FCSTD DOCUMENT  (FreeCAD 0.18R16146 (Git))
Label: full_parametric_model90
License: All rights reserved
LicenseURL: http://en.wikipedia.org/wiki/All_rights_reserved
objects: Part::FeaturePython×27, Sketcher::SketchObject×13, PartDesign::Pad×5, Part::MultiFuse×5, Part::Extrusion×5, Part::Cut×4, App::DocumentObjectGroup×4, Mesh::Feature×4, Part::Mirroring×4, Part::MultiCommon×3, PartDesign::Revolution×3, Part::Feature×3, Part::Compound×2, Part::Fillet×2, Part::Cylinder×1, Spreadsheet::Sheet×1, Part::Sphere×1, Part::Chamfer×1, Part::Loft×1
note: 88 computed .brp shape members not serialized (recipe doc carries the construction recipe); baked Part::Feature solids carry a one-line shape summary decoded from their .brp

FEATURE [Part::Cylinder] Cylinder
  Angle = 360
  AttacherType = Attacher::AttachEngine3D
  Height = 10.3
  Placement = pos=(0,0,-5.15) rot=(0,0,1;0rad)
  Radius = 5.5
  expr: Height = Spreadsheet.SpacerDepth
  expr: Radius = Spreadsheet.SpacerD / 2
FEATURE [Sketcher::SketchObject] Sketch004  label="SpacerTailsSketch"
  MapMode = 5
  expr: Constraints.AxeOutR = Spreadsheet.AxisD / 2 + Spreadsheet.SpacerMinThickness
  expr: Constraints.MaxR = Spreadsheet.SpacerTailsD / 2
  expr: Constraints.AxeR = Spreadsheet.AxisD / 2
  sketch-geometry (15):
    g0: ArcOfCircle CenterX=0 CenterY=0 CenterZ=0 NormalX=0 NormalY=0 NormalZ=1 AngleXU=0 Radius=9 StartAngle=1.8326 EndAngle=2.35619
    g1: Circle [constr] CenterX=0 CenterY=0 CenterZ=0 NormalX=0 NormalY=0 NormalZ=1 AngleXU=0 Radius=9
    g2: ArcOfCircle CenterX=11.5897 CenterY=20.074 CenterZ=0 NormalX=0 NormalY=0 NormalZ=1 AngleXU=0 Radius=17.9795 StartAngle=3.82699 EndAngle=4.55059
    g3: Circle [constr] CenterX=0 CenterY=0 CenterZ=0 NormalX=0 NormalY=0 NormalZ=1 AngleXU=0 Radius=5.2
    g4: LineSegment [constr] StartX=0 StartY=0 StartZ=0 EndX=2.6 EndY=4.50333 EndZ=0
    g5: ArcOfCircle CenterX=0 CenterY=0 CenterZ=0 NormalX=0 NormalY=0 NormalZ=1 AngleXU=0 Radius=9 StartAngle=6.02139 EndAngle=6.54498
    g6: ArcOfCircle CenterX=11.5897 CenterY=-20.074 CenterZ=0 NormalX=0 NormalY=0 NormalZ=1 AngleXU=0 Radius=17.9795 StartAngle=1.7326 EndAngle=2.45619
    g7: LineSegment [constr] StartX=0 StartY=0 StartZ=0 EndX=2.6 EndY=-4.50333 EndZ=0
    g8: ArcOfCircle CenterX=0 CenterY=0 CenterZ=0 NormalX=0 NormalY=0 NormalZ=1 AngleXU=0 Radius=9 StartAngle=3.92699 EndAngle=4.45059
    g9: LineSegment [constr] StartX=0 StartY=0 StartZ=0 EndX=-5.2 EndY=0 EndZ=0
    g10: LineSegment [constr] StartX=0 StartY=0 StartZ=0 EndX=-6.36396 EndY=6.36396 EndZ=0
    g11: ArcOfCircle CenterX=-23.1795 CenterY=2e-12 CenterZ=0 NormalX=0 NormalY=0 NormalZ=1 AngleXU=0 Radius=17.9795 StartAngle=5.92139 EndAngle=6.64498
    g12: LineSegment [constr] StartX=0 StartY=0 StartZ=0 EndX=-6.36396 EndY=-6.36396 EndZ=0
    g13: LineSegment [constr] StartX=0 StartY=0 StartZ=0 EndX=8.69333 EndY=-2.32937 EndZ=0
    g14: Circle CenterX=0 CenterY=0 CenterZ=0 NormalX=0 NormalY=0 NormalZ=1 AngleXU=0 Radius=4
  constraints (43):
    c: Coincident(g0,g-1)
    c: Angle(g0) = 0.523599
    c: Coincident(g1,g-1)
    c: Radius(g1) = 9  'MaxR'
    c: PointOnObject(g0,g1)
    c: Coincident(g2,g0)
    c: PointOnObject(g2,g1)
    c: Coincident(g3,g-1)
    c: Radius(g3) = 5.2  'AxeOutR'
    c: Coincident(g4,g-1)
    c: PointOnObject(g4,g3)
    c: PointOnObject(g4,g2)
    c: Angle(g5) = 0.523599
    c: Coincident(g5,g2)
    c: PointOnObject(g5,g1)
    c: Coincident(g6,g5)
    c: Coincident(g-1,g5)
    c: Coincident(g7,g-1)
    c: PointOnObject(g7,g3)
    c: PointOnObject(g7,g6)
    c: Coincident(g8,g-1)
    c: Coincident(g8,g6)
    c: PointOnObject(g8,g1)
    c: Angle(g8) = 0.523599
    c: Angle(g7,g4) = 2.0944
    c: Coincident(g9,g-1)
    c: PointOnObject(g9,g3)
    c: Angle(g9,g7) = 2.0944
    c: Coincident(g10,g-1)
    c: Coincident(g10,g0)
    c: Angle(g4,g10) = 1.309
    c: Coincident(g11,g8)
    c: Coincident(g11,g0)
    c: PointOnObject(g9,g11)
    c: Coincident(g12,g-1)
    c: Coincident(g12,g8)
    c: Angle(g10,g12) = 1.5708
    c: Coincident(g13,g-1)
    c: Coincident(g13,g5)
    c: Angle(g12,g13) = 2.0944
    c: Coincident(g14,g-1)
    c: Radius(g14) = 4  'AxeR'
    c: Angle(g-1,g9) = 3.14159  'Rotation'
FEATURE [PartDesign::Pad] Pad003  label="SpacerTails"
  Length = 1.4
  Length2 = 100
  Midplane = true
  Profile = -> Sketch004
  Type = 0
  expr: Length = Spreadsheet.SpacerTailsDepth
FEATURE [Spreadsheet::Sheet] Spreadsheet
  cells = A1=Диаметр оси; B1(AxisD)=8; C1=мм; A2=Наружный диаметр подшипника; B2(BearingD)=16; C2=мм; A3=Шаг звена; B3(LinkLength)=40; C3=мм; A4=Минимальный угол складывания; B4(MinLinkAngle)=90; C4=градусов; A5=Толщина подшипника; B5(BearingDepth)=5; C5=мм; A6=Минимальная ширина; B6(MinWidth)=3; C6=мм; A7=Минимальный отступ; B7(MinSpacing)=1; C7=мм; A8=Скругление углов; B8(FIlletR)=2; C8=мм; A9=Держащий край; B9(HoldingEdge)=1.2; C9=мм; A10=Наружный диаметр втулки; B10(SpacerD)=11; C10=мм; A11=Глубина втулки; B11(SpacerDepth)=10.3; C11=мм; A12=Толщина хвостиков втулки; B12(SpacerTailsDepth)=1.4; C12=мм; A13=Диаметр втулки по хвостикам; B13(SpacerTailsD)=18; C13=мм; A14=Минимальная толщина втулки; B14(SpacerMinThickness)=1.2; C14=мм; A15=Клиренс отверстий; B15(HolesClearance)=0.1; C15=мм; A16=Угол оптимального эллипса; B16(OptimalEllipseAngle)=56.33131818071931; C16=градусов; A17=Y-позиция центра направляющей; B17(RailCenterY)==LinkLength * sin(OptimalEllipseAngle)
FEATURE [Part::FeaturePython] Clone007  label="SpacerTailsCutter"  # Draft clone (typed FeaturePython)
  Objects = -> [Pad003]
  Scale = (1,1,8.09286)
  expr: Scale.z = 1.1 * Spreadsheet.SpacerDepth / Spreadsheet.SpacerTailsDepth
FEATURE [Part::MultiCommon] Common
  Shapes = -> [Cylinder,Clone007]
FEATURE [Part::MultiFuse] Fusion  label="SpacerPart"
  Shapes = -> [Common,Pad003]
FEATURE [Sketcher::SketchObject] Sketch013  label="BallBearingInnerRingSketch"
  MapMode = 5
  Placement = pos=(0,0,0) rot=(1,0,0;1.5708rad)
  expr: Constraints[11] = Spreadsheet.AxisD / 2 + (Spreadsheet.BearingD - Spreadsheet.AxisD) / 6
  expr: Constraints[10] = Spreadsheet.AxisD / 2
  expr: Constraints[9] = Spreadsheet.BearingDepth
  sketch-geometry (4):
    g0: LineSegment StartX=4 StartY=2.5 StartZ=0 EndX=5.33333 EndY=2.5 EndZ=0
    g1: LineSegment StartX=5.33333 StartY=2.5 StartZ=0 EndX=5.33333 EndY=-2.5 EndZ=0
    g2: LineSegment StartX=5.33333 StartY=-2.5 StartZ=0 EndX=4 EndY=-2.5 EndZ=0
    g3: LineSegment StartX=4 StartY=-2.5 StartZ=0 EndX=4 EndY=2.5 EndZ=0
  constraints (12):
    c: Coincident(g0,g1)
    c: Coincident(g1,g2)
    c: Coincident(g2,g3)
    c: Coincident(g3,g0)
    c: Horizontal(g0)
    c: Horizontal(g2)
    c: Vertical(g1)
    c: Vertical(g3)
    c: Symmetric(g0,g2,g-1)
    c: DistanceY(g2,g0) = 5
    c: DistanceX(g0) = 4
    c: DistanceX(g0) = 5.33333
FEATURE [PartDesign::Revolution] Revolution  label="BallBearingInnerRing"
  Angle = 360
  Axis = (0,2e-16,1)
  Base = (0,0,0)
  Placement = pos=(0,0,0) rot=(1,0,0;1.5708rad)
  Profile = -> Sketch013
  ReferenceAxis = -> Sketch013 [V_Axis]
  Reversed = true
FEATURE [Sketcher::SketchObject] Sketch014  label="BallBearingInnerRingSketch001"
  MapMode = 5
  Placement = pos=(0,0,0) rot=(1,0,0;1.5708rad)
  expr: Constraints[11] = Spreadsheet.BearingD / 2 - (Spreadsheet.BearingD - Spreadsheet.AxisD) / 6
  expr: Constraints[10] = Spreadsheet.BearingD / 2
  expr: Constraints[9] = Spreadsheet.BearingDepth
  sketch-geometry (4):
    g0: LineSegment StartX=8 StartY=2.5 StartZ=0 EndX=6.66667 EndY=2.5 EndZ=0
    g1: LineSegment StartX=6.66667 StartY=2.5 StartZ=0 EndX=6.66667 EndY=-2.5 EndZ=0
    g2: LineSegment StartX=6.66667 StartY=-2.5 StartZ=0 EndX=8 EndY=-2.5 EndZ=0
    g3: LineSegment StartX=8 StartY=-2.5 StartZ=0 EndX=8 EndY=2.5 EndZ=0
  constraints (12):
    c: Coincident(g0,g1)
    c: Coincident(g1,g2)
    c: Coincident(g2,g3)
    c: Coincident(g3,g0)
    c: Horizontal(g0)
    c: Horizontal(g2)
    c: Vertical(g1)
    c: Vertical(g3)
    c: Symmetric(g0,g2,g-1)
    c: DistanceY(g2,g0) = 5
    c: DistanceX(g0) = 8
    c: DistanceX(g0) = 6.66667
FEATURE [PartDesign::Revolution] Revolution001  label="BallBearingOuterRing"
  Angle = 360
  Axis = (0,2e-16,1)
  Base = (0,0,0)
  Placement = pos=(0,0,0) rot=(1,0,0;1.5708rad)
  Profile = -> Sketch014
  ReferenceAxis = -> Sketch014 [V_Axis]
  Reversed = true
FEATURE [Sketcher::SketchObject] Sketch015  label="BallBearingGrooveTorusSketch"
  MapMode = 5
  Placement = pos=(0,0,0) rot=(1,0,0;1.5708rad)
  expr: Constraints[1] = 2 * (Spreadsheet.BearingD - Spreadsheet.AxisD) / 12
  sketch-geometry (1):
    g0: Circle CenterX=6 CenterY=0 CenterZ=0 NormalX=0 NormalY=0 NormalZ=1 AngleXU=0 Radius=1.33333
  constraints (3):
    c: PointOnObject(g0,g-1)
    c: Radius(g0) = 1.33333
    c: DistanceX(g0) = 6
FEATURE [PartDesign::Revolution] Revolution002  label="BallBearingGrooveTorus"
  Angle = 360
  Axis = (0,2e-16,1)
  Base = (0,0,0)
  Placement = pos=(0,0,0) rot=(1,0,0;1.5708rad)
  Profile = -> Sketch015
  ReferenceAxis = -> Sketch015 [V_Axis]
  Reversed = true
FEATURE [Part::MultiFuse] Fusion001  label="BallBearingRings"
  Shapes = -> [Revolution001,Revolution]
FEATURE [Part::Cut] Cut  label="BallBearingRingsWithGroove"
  Base = -> Fusion001
  Tool = -> Revolution002
FEATURE [Part::Sphere] Sphere
  Angle1 = -90
  Angle2 = 90
  Angle3 = 360
  AttacherType = Attacher::AttachEngine3D
  Placement = pos=(6,0,0) rot=(0,0,1;0rad)
  Radius = 1.33333
  expr: Placement.Base.x = (Spreadsheet.BearingD + Spreadsheet.AxisD) / 4
FEATURE [Part::FeaturePython] Array  # Draft array (typed FeaturePython)
  Angle = 360
  ArrayType = 1
  Axis = (0,0,1)
  Base = -> Sphere
  Center = (0,0,0)
  Fuse = false
  IntervalAxis = (0,0,0)
  IntervalX = (1,0,0)
  IntervalY = (0,1,0)
  IntervalZ = (0,0,0)
  NumberPolar = 10
  NumberX = 2
  NumberY = 2
  NumberZ = 1
FEATURE [Part::MultiFuse] Fusion002  label="BallBearing"
  Shapes = -> [Array,Cut]
FEATURE [App::DocumentObjectGroup] Group  label="StockParts"
  Group = -> [Fusion,Fusion002]
FEATURE [Part::Feature] Path  label="Path16D40L"
  Placement = pos=(-54.1756,58.5806,12.8) rot=(0,0,1;0rad)
  shape: bbox 108.4 x 50.58 x 2e-07 mm, 0 faces, 0 solids (baked)
  expr: Placement.Base.y = 2 * Spreadsheet.RailCenterY - 16 / 2
  expr: Placement.Base.x = 16 / 2 - Spreadsheet.LinkLength * (1 + cos(Spreadsheet.OptimalEllipseAngle))
FEATURE [Part::FeaturePython] Clone023  label="CenterBearing"  # Draft clone (typed FeaturePython)
  Objects = -> [Fusion002]
  Scale = (1,1,1)
FEATURE [Part::FeaturePython] Clone024  label="LeftBearing"  # Draft clone (typed FeaturePython)
  Objects = -> [Fusion002]
  Placement = pos=(0,0,15.3) rot=(0,0,1;0rad)
  Scale = (1,1,1)
  expr: Placement.Base.z = Spreadsheet.SpacerDepth + Spreadsheet.BearingDepth
FEATURE [Part::FeaturePython] Clone025  label="RightBearing"  # Draft clone (typed FeaturePython)
  Objects = -> [Fusion002]
  Placement = pos=(0,0,-15.3) rot=(0,0,1;0rad)
  Scale = (1,1,1)
  expr: Placement.Base.z = -Spreadsheet.SpacerDepth - Spreadsheet.BearingDepth
FEATURE [Part::FeaturePython] Clone026  label="LeftSpacer"  # Draft clone (typed FeaturePython)
  Objects = -> [Fusion]
  Placement = pos=(0,0,7.65) rot=(0,0,1;0rad)
  Scale = (1,1,1)
  expr: Placement.Base.z = (Spreadsheet.SpacerDepth + Spreadsheet.BearingDepth) / 2
FEATURE [Part::FeaturePython] Clone027  label="RightSpacer"  # Draft clone (typed FeaturePython)
  Objects = -> [Fusion]
  Placement = pos=(0,0,-7.65) rot=(0,0,1;0rad)
  Scale = (1,1,1)
  expr: Placement.Base.z = -0.5 * (Spreadsheet.SpacerDepth + Spreadsheet.BearingDepth)
FEATURE [Sketcher::SketchObject] Sketch012007  label="TrussSketch"
  MapMode = 5
  Placement = pos=(0,0,0) rot=(1,0,0;1.5708rad)
  expr: Constraints[36] = 0.5 * (Spreadsheet.BearingDepth + Spreadsheet.SpacerDepth + Spreadsheet.SpacerTailsDepth) + Spreadsheet.MinSpacing
  expr: Constraints[35] = Spreadsheet.HoldingEdge * 2
  sketch-geometry (14):
    g0: LineSegment StartX=11.0471 StartY=9.35 StartZ=0 EndX=1.69706 EndY=0 EndZ=0
    g1: LineSegment StartX=1.69706 StartY=0 StartZ=0 EndX=11.0471 EndY=-9.35 EndZ=0
    g2: LineSegment StartX=11.0471 StartY=-9.35 StartZ=0 EndX=11.0471 EndY=9.35 EndZ=0
    g3: LineSegment StartX=-1.69706 StartY=0 StartZ=0 EndX=-11.0471 EndY=9.35 EndZ=0
    g4: LineSegment StartX=-11.0471 StartY=9.35 StartZ=0 EndX=-11.0471 EndY=-9.35 EndZ=0
    g5: LineSegment StartX=-11.0471 StartY=-9.35 StartZ=0 EndX=-1.69706 EndY=0 EndZ=0
    g6: LineSegment StartX=0 StartY=1.69706 StartZ=0 EndX=7.65294 EndY=9.35 EndZ=0
    g7: LineSegment StartX=7.65294 StartY=9.35 StartZ=0 EndX=-7.65294 EndY=9.35 EndZ=0
    g8: LineSegment StartX=-7.65294 StartY=9.35 StartZ=0 EndX=0 EndY=1.69706 EndZ=0
    g9: LineSegment [constr] StartX=11.0471 StartY=9.35 StartZ=0 EndX=7.65294 EndY=9.35 EndZ=0
    g10: LineSegment [constr] StartX=-1.69706 StartY=0 StartZ=0 EndX=0 EndY=1.69706 EndZ=0
    g11: LineSegment StartX=-7.65294 StartY=-9.35 StartZ=0 EndX=0 EndY=-1.69706 EndZ=0
    g12: LineSegment StartX=0 StartY=-1.69706 StartZ=0 EndX=7.65294 EndY=-9.35 EndZ=0
    g13: LineSegment StartX=7.65294 StartY=-9.35 StartZ=0 EndX=-7.65294 EndY=-9.35 EndZ=0
  constraints (37):
    c: PointOnObject(g0,g-1)
    c: Coincident(g0,g1)
    c: Coincident(g1,g2)
    c: Coincident(g2,g0)
    c: Perpendicular(g1,g0)
    c: Vertical(g2)
    c: Equal(g1,g0)
    c: Coincident(g3,g4)
    c: Vertical(g4)
    c: Coincident(g4,g5)
    c: Coincident(g5,g3)
    c: Equal(g3,g5)
    c: Perpendicular(g5,g3)
    c: Equal(g4,g2)
    c: PointOnObject(g6,g-2)
    c: Coincident(g6,g7)
    c: Horizontal(g7)
    c: Coincident(g7,g8)
    c: Coincident(g8,g6)
    c: Perpendicular(g6,g8)
    c: Equal(g8,g6)
    c: Coincident(g9,g0)
    c: Coincident(g9,g6)
    c: Horizontal(g9)
    c: Coincident(g10,g3)
    c: Coincident(g10,g6)
    c: Symmetric(g0,g3,g-1)
    c: Parallel(g6,g10)
    c: Coincident(g12,g13)
    c: Horizontal(g13)
    c: Coincident(g13,g11)
    c: Coincident(g11,g12)
    c: Equal(g11,g12)
    c: Symmetric(g11,g6,g-1)
    c: Symmetric(g12,g6,g-1)
    c: Distance(g10) = 2.4
    c: DistanceY(g0) = 9.35
FEATURE [Part::Compound] Compound  label="AxleAssembly"
  Links = -> [Clone023,Clone024,Clone025,Clone026,Clone027]
FEATURE [Sketcher::SketchObject] Sketch012008  label="RailProfile"
  MapMode = 5
  Placement = pos=(0,0,0) rot=(0.57735,0.57735,0.57735;2.0944rad)
  expr: Constraints[48] = 0.5 * Spreadsheet.BearingDepth + 4 * Spreadsheet.MinSpacing
  expr: Constraints[37] = 0.5 * Spreadsheet.SpacerTailsD + 4 * Spreadsheet.MinSpacing
  expr: Constraints[35] = 2 * Spreadsheet.HoldingEdge
  expr: Constraints[15] = Spreadsheet.SpacerDepth + 0.5 * Spreadsheet.BearingDepth
  expr: Constraints[14] = 0.5 * Spreadsheet.BearingD
  expr: Constraints[36] = 0.5 * (Spreadsheet.SpacerDepth - Spreadsheet.SpacerTailsDepth) - Spreadsheet.MinSpacing
  sketch-geometry (17):
    g0: LineSegment StartX=8 StartY=15.3 StartZ=0 EndX=8 EndY=12.8 EndZ=0
    g1: LineSegment StartX=8 StartY=12.8 StartZ=0 EndX=6.5 EndY=12.254 EndZ=0
    g2: LineSegment StartX=6.5 StartY=12.254 StartZ=0 EndX=6.5 EndY=9.35 EndZ=0
    g3: LineSegment StartX=6.5 StartY=9.35 StartZ=0 EndX=10.15 EndY=9.35 EndZ=0
    g4: LineSegment StartX=13 StartY=6.5 StartZ=0 EndX=13 EndY=0 EndZ=0
    g5: LineSegment StartX=8 StartY=15.3 StartZ=0 EndX=15.4 EndY=15.3 EndZ=0
    g6: LineSegment StartX=15.4 StartY=15.3 StartZ=0 EndX=15.4 EndY=0 EndZ=0
    g7: LineSegment StartX=15.4 StartY=0 StartZ=0 EndX=15.4 EndY=-15.3 EndZ=0
    g8: LineSegment StartX=15.4 StartY=-15.3 StartZ=0 EndX=8 EndY=-15.3 EndZ=0
    g9: LineSegment StartX=8 StartY=-15.3 StartZ=0 EndX=8 EndY=-12.8 EndZ=0
    g10: LineSegment StartX=8 StartY=-12.8 StartZ=0 EndX=6.5 EndY=-12.254 EndZ=0
    g11: LineSegment StartX=6.5 StartY=-12.254 StartZ=0 EndX=6.5 EndY=-9.35 EndZ=0
    g12: LineSegment StartX=6.5 StartY=-9.35 StartZ=0 EndX=10.15 EndY=-9.35 EndZ=0
    g13: LineSegment StartX=13 StartY=-6.5 StartZ=0 EndX=13 EndY=0 EndZ=0
    g14: LineSegment StartX=13 StartY=6.5 StartZ=0 EndX=10.15 EndY=9.35 EndZ=0
    g15: LineSegment StartX=13 StartY=-6.5 StartZ=0 EndX=10.15 EndY=-9.35 EndZ=0
    g16: LineSegment [constr] StartX=6.5 StartY=9.35 StartZ=0 EndX=6.5 EndY=-9.35 EndZ=0
  constraints (49):
    c: Vertical(g0)
    c: Coincident(g0,g1)
    c: Coincident(g1,g2)
    c: Vertical(g2)
    c: Coincident(g2,g3)
    c: Horizontal(g3)
    c: PointOnObject(g4,g-1)
    c: Vertical(g4)
    c: Horizontal(g5)
    c: Coincident(g5,g6)
    c: PointOnObject(g6,g-1)
    c: Vertical(g6)
    c: Coincident(g0,g5)
    c: Angle(g0,g1) = 1.91986
    c: DistanceX(g0) = 8
    c: DistanceY(g0) = 12.8
    c: DistanceX(g2) = 6.5
    c: DistanceY(g0,g0) = 2.5
    c: Coincident(g6,g7)
    c: Vertical(g7)
    c: Coincident(g7,g8)
    c: Horizontal(g8)
    c: Coincident(g8,g9)
    c: Vertical(g9)
    c: Coincident(g9,g10)
    c: Coincident(g10,g11)
    c: Vertical(g11)
    c: Coincident(g11,g12)
    c: Horizontal(g12)
    c: Vertical(g13)
    c: Coincident(g4,g13)
    c: Equal(g7,g6)
    c: Equal(g12,g3)
    c: Symmetric(g9,g0,g-1)
    c: Equal(g11,g2)
    c: DistanceX(g4,g6) = 2.4
    c: DistanceY(g2,g0) = 3.45
    c: DistanceX(g4) = 13
    c: Equal(g13,g4)
    c: Coincident(g14,g4)
    c: Coincident(g14,g3)
    c: Coincident(g15,g13)
    c: Coincident(g15,g12)
    c: Angle(g14,g4) = 2.35619
    c: Angle(g13,g15) = 2.35619
    c: Coincident(g16,g2)
    c: Coincident(g16,g11)
    c: Vertical(g16)
    c: DistanceY(g4,g4) = 6.5
FEATURE [PartDesign::Pad] Pad004002016  label="TestRailBody"
  Length = 132
  Length2 = 100
  Midplane = true
  Placement = pos=(0,0,0) rot=(0.57735,0.57735,0.57735;2.0944rad)
  Profile = -> Sketch012008
  Type = 0
FEATURE [Sketcher::SketchObject] Sketch012009  label="LinkSide"
  MapMode = 5
  expr: Constraints[7] = Spreadsheet.BearingD / 2 + 0.8 * Spreadsheet.HolesClearance
  expr: Constraints[9] = 0.5 * Spreadsheet.BearingD + 2 * Spreadsheet.HoldingEdge
  expr: Constraints[33] = Spreadsheet.HoldingEdge
  expr: Constraints[4] = 0.5 * Spreadsheet.SpacerTailsD
  expr: Constraints[32] = 0.5 * Spreadsheet.BearingD + 2 * Spreadsheet.HoldingEdge + 1.5 * Spreadsheet.MinSpacing
  sketch-geometry (12):
    g0: ArcOfCircle CenterX=0 CenterY=0 CenterZ=0 NormalX=0 NormalY=0 NormalZ=1 AngleXU=0 Radius=9 StartAngle=1.5708 EndAngle=3.92699
    g1: LineSegment StartX=-9.307e-13 StartY=9 StartZ=0 EndX=11.9 EndY=9 EndZ=0
    g2: Circle CenterX=0 CenterY=0 CenterZ=0 NormalX=0 NormalY=0 NormalZ=1 AngleXU=0 Radius=5.55
    g3: Circle CenterX=40 CenterY=0 CenterZ=0 NormalX=0 NormalY=0 NormalZ=1 AngleXU=0 Radius=8.08
    g4: ArcOfCircle CenterX=40 CenterY=0 CenterZ=0 NormalX=0 NormalY=0 NormalZ=1 AngleXU=0 Radius=10.4 StartAngle=5.49779 EndAngle=7.85398
    g5: LineSegment StartX=-6.36396 StartY=-6.36396 StartZ=0 EndX=-1.72792 EndY=-11 EndZ=0
    g6: LineSegment StartX=43.7078 StartY=-11 StartZ=0 EndX=-1.72792 EndY=-11 EndZ=0
    g7: LineSegment StartX=47.3539 StartY=-7.35391 StartZ=0 EndX=43.7078 EndY=-11 EndZ=0
    g8: LineSegment StartX=40 StartY=10.4 StartZ=0 EndX=14.3 EndY=10.4 EndZ=0
    g9: ArcOfCircle CenterX=14.3 CenterY=9.02144 CenterZ=0 NormalX=0 NormalY=0 NormalZ=1 AngleXU=0 Radius=1.37856 StartAngle=1.5708 EndAngle=2.62695
    g10: ArcOfCircle CenterX=11.9 CenterY=10.3786 CenterZ=0 NormalX=0 NormalY=0 NormalZ=1 AngleXU=0 Radius=1.37856 StartAngle=4.71239 EndAngle=5.76854
    g11: GeomPoint [constr] X=50.4 Y=0 Z=0
  constraints (34):
    c: Coincident(g0,g-1)
    c: PointOnObject(g0,g-2)
    c: Coincident(g1,g0)
    c: Horizontal(g1)
    c: Radius(g0) = 9
    c: Coincident(g2,g-1)
    c: Radius(g2) = 5.55
    c: Radius(g3) = 8.08
    c: Coincident(g4,g3)
    c: Radius(g4) = 10.4
    c: PointOnObject(g3,g-1)
    c: DistanceX(g-1,g3) = 40
    c: Coincident(g5,g0)
    c: Tangent(g5,g0)
    c: Horizontal(g6)
    c: Coincident(g6,g5)
    c: Angle(g6,g5) = 2.35619
    c: Coincident(g7,g4)
    c: Tangent(g7,g4)
    c: Coincident(g7,g6)
    c: Angle(g7,g6) = 2.35619
    c: DistanceY(g6) = -11
    c: Coincident(g8,g4)
    c: Horizontal(g8)
    c: Tangent(g4,g8)
    c: Coincident(g9,g8)
    c: Coincident(g10,g9)
    c: Coincident(g10,g1)
    c: Tangent(g10,g9)
    c: Tangent(g9,g8)
    c: Tangent(g10,g1)
    c: Equal(g9,g10)
    c: DistanceX(g1) = 11.9
    c: DistanceX(g1,g9) = 1.2
FEATURE [PartDesign::Pad] Pad004002017  label="LinkSideExtraction"
  Length = 50
  Length2 = 100
  Midplane = true
  Profile = -> Sketch012009
  Type = 0
FEATURE [Sketcher::SketchObject] Sketch012010  label="LinkBottom"
  MapMode = 5
  Placement = pos=(0,0,0) rot=(1,0,0;1.5708rad)
  expr: Constraints[20] = 0.5 * Spreadsheet.BearingD + 2 * Spreadsheet.HoldingEdge + 1.5 * Spreadsheet.MinSpacing
  expr: Constraints[49] = 2 * Spreadsheet.HoldingEdge
  expr: Constraints[23] = 0.5 * Spreadsheet.BearingDepth + 1.5 * Spreadsheet.MinSpacing
  expr: Constraints[19] = -0.5 * Spreadsheet.SpacerTailsD
  expr: Constraints[26] = 0.5 * Spreadsheet.BearingD + 2 * Spreadsheet.HoldingEdge
  expr: Constraints[31] = 0.5 * Spreadsheet.BearingDepth + 0.5 * (Spreadsheet.SpacerDepth - Spreadsheet.SpacerTailsDepth)
  expr: Constraints[22] = Spreadsheet.BearingDepth
  sketch-geometry (21):
    g0: LineSegment StartX=50.4 StartY=2.5 StartZ=0 EndX=50.4 EndY=-2.5 EndZ=0
    g1: LineSegment StartX=50.4 StartY=-2.5 StartZ=0 EndX=29.6 EndY=-2.5 EndZ=0
    g2: LineSegment StartX=29.6 StartY=2.5 StartZ=0 EndX=13.1 EndY=6.95 EndZ=0
    g3: LineSegment StartX=13.1 StartY=6.95 StartZ=0 EndX=-9 EndY=6.95 EndZ=0
    g4: LineSegment StartX=-9 StartY=6.95 StartZ=0 EndX=-9 EndY=4 EndZ=0
    g5: LineSegment StartX=-9 StartY=4 StartZ=0 EndX=11.9 EndY=4 EndZ=0
    g6: LineSegment StartX=11.9 StartY=4 StartZ=0 EndX=11.9 EndY=-4 EndZ=0
    g7: LineSegment StartX=11.9 StartY=-4 StartZ=0 EndX=-9 EndY=-4 EndZ=0
    g8: LineSegment StartX=-9 StartY=-4 StartZ=0 EndX=-9 EndY=-6.95 EndZ=0
    g9: LineSegment StartX=-9 StartY=-6.95 StartZ=0 EndX=13.1 EndY=-6.95 EndZ=0
    g10: LineSegment StartX=13.1 StartY=-6.95 StartZ=0 EndX=29.6 EndY=-2.5 EndZ=0
    g11: LineSegment StartX=50.4 StartY=2.5 StartZ=0 EndX=40 EndY=2.5 EndZ=0
    g12: LineSegment StartX=40 StartY=2.5 StartZ=0 EndX=29.6 EndY=2.5 EndZ=0
    g13: LineSegment StartX=14.3 StartY=4 StartZ=0 EndX=14.3 EndY=-4 EndZ=0
    g14: LineSegment StartX=14.3 StartY=-4 StartZ=0 EndX=27.0794 EndY=-0.553433 EndZ=0
    g15: LineSegment StartX=27.0794 StartY=0.553432 StartZ=0 EndX=14.3 EndY=4 EndZ=0
    g16: LineSegment [constr] StartX=11.9 StartY=4 StartZ=0 EndX=14.3 EndY=4 EndZ=0
    g17: LineSegment [constr] StartX=29.6 StartY=2.5 StartZ=0 EndX=27.0794 EndY=0.553432 EndZ=0
    g18: LineSegment [constr] StartX=14.3 StartY=4 StartZ=0 EndX=13.1 EndY=6.95 EndZ=0
    g19: LineSegment [constr] StartX=13.1 StartY=6.95 StartZ=0 EndX=11.9 EndY=4 EndZ=0
    g20: ArcOfCircle CenterX=26.9301 CenterY=0 CenterZ=0 NormalX=0 NormalY=0 NormalZ=1 AngleXU=0 Radius=0.573208 StartAngle=4.97582 EndAngle=7.59054
  constraints (56):
    c: Vertical(g0)
    c: Coincident(g0,g1)
    c: Horizontal(g1)
    c: Coincident(g2,g3)
    c: Horizontal(g3)
    c: Coincident(g3,g4)
    c: Vertical(g4)
    c: Coincident(g4,g5)
    c: Horizontal(g5)
    c: Coincident(g5,g6)
    c: Vertical(g6)
    c: Coincident(g6,g7)
    c: Horizontal(g7)
    c: Coincident(g7,g8)
    c: Coincident(g8,g9)
    c: Symmetric(g7,g4,g-1)
    c: Symmetric(g8,g3,g-1)
    c: Coincident(g9,g10)
    c: Symmetric(g9,g2,g-1)
    c: DistanceX(g3) = -9
    c: DistanceX(g5) = 11.9
    c: Symmetric(g1,g12,g-1)
    c: DistanceY(g0,g0) = 5
    c: DistanceY(g-1,g4) = 4
    c: Horizontal(g11)
    c: DistanceX(g11) = 40
    c: DistanceX(g11,g11) = 10.4
    c: Coincident(g0,g11)
    c: Coincident(g12,g11)
    c: Horizontal(g12)
    c: Equal(g11,g12)
    c: DistanceY(g3) = 6.95
    c: Coincident(g10,g1)
    c: Coincident(g2,g12)
    c: Vertical(g13)
    c: Coincident(g13,g14)
    c: Coincident(g15,g13)
    c: Coincident(g16,g5)
    c: Coincident(g16,g13)
    c: Horizontal(g16)
    c: Parallel(g15,g2)
    c: Parallel(g10,g14)
    c: Coincident(g17,g2)
    c: Coincident(g18,g2)
    c: Coincident(g19,g2)
    c: Coincident(g19,g5)
    c: Equal(g19,g18)
    c: Equal(g18,g17)
    c: Coincident(g18,g13)
    c: DistanceX(g16,g16) = 2.4
    c: PointOnObject(g20,g-1)
    c: Coincident(g20,g15)
    c: Coincident(g20,g14)
    c: Tangent(g20,g15)
    c: Coincident(g17,g15)
    c: Tangent(g14,g20,g14) = -1.5708
FEATURE [PartDesign::Pad] Pad004002018  label="LinkBottomExraction"
  Length = 50
  Length2 = 100
  Midplane = true
  Placement = pos=(0,0,0) rot=(1,0,0;1.5708rad)
  Profile = -> Sketch012010
  Type = 0
FEATURE [Part::MultiCommon] Common001  label="WholeLinkSharp"
  Shapes = -> [Pad004002017,Pad004002018]
FEATURE [Part::Fillet] Fillet002  label="WholeLinkSomeFillets"
  Base = -> Common001
  Edges = 8 edges r=1: [Edge7,Edge20,Edge25,Edge49,Edge53,Edge71,Edge82,Edge84]
FEATURE [Part::Chamfer] Chamfer  label="WholeLinkPart"
  Base = -> Fillet002
  Edges = 8 edges r=0.5: [Edge12,Edge29,Edge67,Edge76,Edge84,Edge85,Edge90,Edge99]
FEATURE [Part::FeaturePython] Clone028  label="WholeLink7"  # Draft clone (typed FeaturePython)
  Objects = -> [Chamfer]
  Placement = pos=(-40,0,0) rot=(0,0,1;0rad)
  Scale = (1,1,1)
  expr: Placement.Base.x = -Spreadsheet.LinkLength
FEATURE [Mesh::Feature] Mesh001  label="WholeLink-v3"
FEATURE [Mesh::Feature] Mesh002  label="WholeLink-v4"
FEATURE [Part::Feature] Path001  label="Path12D40L"
  Placement = pos=(-56.18,60.5806,12.254) rot=(0,0,1;0rad)
  shape: bbox 112.4 x 54.58 x 2e-07 mm, 0 faces, 0 solids (baked)
  expr: Placement.Base.y = 2 * Spreadsheet.RailCenterY - 12 / 2
  expr: Placement.Base.x = 12 / 2 - Spreadsheet.LinkLength * (1 + cos(Spreadsheet.OptimalEllipseAngle))
FEATURE [Part::FeaturePython] Clone029  label="InnerPath12D40L"  # Draft clone (typed FeaturePython)
  Objects = -> [Path001]
  Placement = pos=(-56.18,60.5806,9.354) rot=(0,0,1;0rad)
  Scale = (1,1,1)
  expr: Placement.Base.y = Path12D40L.Placement.Base.y
  expr: Placement.Base.x = Path12D40L.Placement.Base.x
  expr: Placement.Base.z = 12.254 - 2.9
FEATURE [Part::FeaturePython] Clone030  label="OuterPath16D40L"  # Draft clone (typed FeaturePython)
  Objects = -> [Path]
  Placement = pos=(-54.1756,58.5806,15.3) rot=(0,0,1;0rad)
  Scale = (1,1,1)
  expr: Placement.Base.y = Path16D40L.Placement.Base.y
  expr: Placement.Base.x = Path16D40L.Placement.Base.x
  expr: Placement.Base.z = 12.8 + 2.5
FEATURE [Part::Loft] Loft  label="Rail"
  Closed = false
  MaxDegree = 5
  Ruled = true
  Sections = -> [Clone030,Path,Path001,Clone029]
  Solid = true
FEATURE [Part::FeaturePython] Clone031  label="WholeLink1"  # Draft clone (typed FeaturePython)
  Objects = -> [Chamfer]
  Placement = pos=(40,0,0) rot=(0,0,1;0.983167rad)
  Scale = (1,1,1)
  expr: Placement.Rotation.Angle = Spreadsheet.OptimalEllipseAngle
FEATURE [Part::FeaturePython] Clone032  label="WholeLink2"  # Draft clone (typed FeaturePython)
  Objects = -> [Chamfer]
  Placement = pos=(62.1756,33.2903,0) rot=(0,0,1;2.15843rad)
  Scale = (1,1,1)
  expr: Placement.Rotation.Angle = 180 - Spreadsheet.OptimalEllipseAngle
  expr: Placement.Base.y = 40 * sin(Spreadsheet.OptimalEllipseAngle)
  expr: Placement.Base.x = 40 * (1 + cos(Spreadsheet.OptimalEllipseAngle))
FEATURE [Part::FeaturePython] Clone033  label="Axle1"  # Draft clone (typed FeaturePython)
  Objects = -> [Compound]
  Placement = pos=(40,0,0) rot=(0,0,1;0rad)
  Scale = (1,1,1)
FEATURE [Part::FeaturePython] Clone034  label="Axle2"  # Draft clone (typed FeaturePython)
  Objects = -> [Compound]
  Placement = pos=(62.1756,33.2903,0) rot=(0,0,1;0rad)
  Scale = (1,1,1)
  expr: Placement.Base.y = Spreadsheet.LinkLength * sin(Spreadsheet.OptimalEllipseAngle)
  expr: Placement.Base.x = Spreadsheet.LinkLength * (1 + cos(Spreadsheet.OptimalEllipseAngle))
FEATURE [Part::FeaturePython] Clone035  label="Axle3"  # Draft clone (typed FeaturePython)
  Objects = -> [Compound]
  Placement = pos=(40,66.5806,0) rot=(0,0,1;0rad)
  Scale = (1,1,1)
  expr: Placement.Base.y = 2 * 40 * sin(Spreadsheet.OptimalEllipseAngle)
FEATURE [Sketcher::SketchObject] Sketch012011  label="kinematics"
  MapMode = 5
  expr: Constraints[18] = Spreadsheet.LinkLength
  expr: Constraints[4] = 2 * Spreadsheet.LinkLength * sin(Spreadsheet.OptimalEllipseAngle)
  sketch-geometry (13):
    g0: LineSegment StartX=12.2011 StartY=0 StartZ=0 EndX=52.2011 EndY=5.49186 EndZ=0
    g1: LineSegment StartX=52.2011 StartY=5.49186 StartZ=0 EndX=60.7717 EndY=44.9469 EndZ=0
    g2: Ellipse [constr] CenterX=40 CenterY=33.2903 CenterZ=0 NormalX=0 NormalY=0 NormalZ=1 MajorRadius=33.2903 MinorRadius=22.1756 AngleXU=-1.5708
    g3: LineSegment [constr] StartX=40 StartY=-1.84e-14 StartZ=0 EndX=40 EndY=66.5806 EndZ=0
    g4: LineSegment [constr] StartX=62.1756 StartY=33.2903 StartZ=0 EndX=17.8244 EndY=33.2903 EndZ=0
    g5: GeomPoint [constr] X=40 Y=8.46114 Z=0
    g6: GeomPoint [constr] X=40 Y=58.1194 Z=0
    g7: Circle CenterX=12.2011 CenterY=0 CenterZ=0 NormalX=0 NormalY=0 NormalZ=1 AngleXU=0 Radius=12.4
    g8: LineSegment [constr] StartX=0 StartY=66.5806 StartZ=0 EndX=40 EndY=66.5806 EndZ=0
    g9: Circle CenterX=52.2011 CenterY=5.49186 CenterZ=0 NormalX=0 NormalY=0 NormalZ=1 AngleXU=0 Radius=12.4
    g10: LineSegment StartX=10.5144 StartY=12.2848 StartZ=0 EndX=50.5144 EndY=17.7766 EndZ=0
    g11: Circle CenterX=60.7717 CenterY=44.9469 CenterZ=0 NormalX=0 NormalY=0 NormalZ=1 AngleXU=0 Radius=12.4
    g12: LineSegment StartX=40.0837 StartY=8.12406 StartZ=0 EndX=48.6543 EndY=47.5792 EndZ=0
  constraints (25):
    c: InternalAlignment(g3-g6 -> g2) x4
    c: DistanceY(g3,g3) = 66.5806
    c: Coincident(g7,g0)
    c: Radius(g7) = 12.4
    c: Equal(g0,g1)
    c: PointOnObject(g8,g-2)
    c: Coincident(g8,g3)
    c: Horizontal(g8)
    c: Equal(g9,g7)
    c: Tangent(g10,g7)
    c: Tangent(g10,g9)
    c: Coincident(g11,g1)
    c: Equal(g11,g7)
    c: Tangent(g12,g11)
    c: Tangent(g12,g9)
    c: DistanceX(g0,g0) = 40
    c: PointOnObject(g1,g2)
    c: Coincident(g1,g0)
    c: PointOnObject(g0,g2)
    c: PointOnObject(g0,g-1)
    c: Coincident(g9,g0)
    c: PointOnObject(g10,g9)
    c: Equal(g10,g0)
    c: Equal(g12,g1)
    c: PointOnObject(g12,g11)
FEATURE [Sketcher::SketchObject] Sketch012013  label="RailCutoutSketch"
  MapMode = 5
  expr: Constraints[116] = 0.5 * (Spreadsheet.AxisD + Spreadsheet.HolesClearance)
  expr: Constraints[72] = 3 * Spreadsheet.HoldingEdge
  expr: Constraints[6] = Spreadsheet.LinkLength * sin(Spreadsheet.OptimalEllipseAngle)
  expr: Constraints[4] = 2 * Spreadsheet.LinkLength
  sketch-geometry (47):
    g0: LineSegment [constr] StartX=40 StartY=24.4135 StartZ=0 EndX=25.0019 EndY=15.3639 EndZ=0
    g1: LineSegment [constr] StartX=-40 StartY=33.2903 StartZ=0 EndX=40 EndY=33.2903 EndZ=0
    g2: Circle CenterX=-32.5 CenterY=33.2903 CenterZ=0 NormalX=0 NormalY=0 NormalZ=1 AngleXU=0 Radius=4.05
    g3: Circle CenterX=0 CenterY=33.2903 CenterZ=0 NormalX=0 NormalY=0 NormalZ=1 AngleXU=0 Radius=4.05
    g4: Circle [constr] CenterX=-32.5 CenterY=33.2903 CenterZ=0 NormalX=0 NormalY=0 NormalZ=1 AngleXU=0 Radius=7.5
    g5: Circle [constr] CenterX=0 CenterY=33.2903 CenterZ=0 NormalX=0 NormalY=0 NormalZ=1 AngleXU=0 Radius=7.5
    g6: LineSegment StartX=-40.5065 StartY=37.8199 StartZ=0 EndX=-47.1952 EndY=40.9886 EndZ=0
    g7: LineSegment StartX=-37.8459 StartY=40.7764 StartZ=0 EndX=-43.218 EndY=49.584 EndZ=0
    g8: LineSegment StartX=-26.362 StartY=40.1419 StartZ=0 EndX=-20.3696 EndY=53.0133 EndZ=0
    g9: LineSegment StartX=-23.6979 StartY=35.9631 StartZ=0 EndX=-18.05 EndY=35.9631 EndZ=0
    g10: LineSegment StartX=-18.05 StartY=35.9631 StartZ=0 EndX=-18.05 EndY=53.0133 EndZ=0
    g11: LineSegment [constr] StartX=-39.7609 StartY=53.0133 StartZ=0 EndX=-43.218 EndY=49.584 EndZ=0
    g12: LineSegment [constr] StartX=-43.218 StartY=49.584 StartZ=0 EndX=-47.1952 EndY=40.9886 EndZ=0
    g13: LineSegment StartX=-14.45 StartY=35.9631 StartZ=0 EndX=-14.45 EndY=53.0133 EndZ=0
    g14: LineSegment StartX=-8.8021 StartY=35.9631 StartZ=0 EndX=-14.45 EndY=35.9631 EndZ=0
    g15: LineSegment [constr] StartX=-14.45 StartY=35.9631 StartZ=0 EndX=-18.05 EndY=35.9631 EndZ=0
    g16: LineSegment StartX=-30.2667 StartY=42.214 StartZ=0 EndX=-25.2391 EndY=53.0133 EndZ=0
    g17: LineSegment StartX=-25.2391 StartY=53.0133 StartZ=0 EndX=-39.7609 EndY=53.0133 EndZ=0
    g18: LineSegment StartX=-39.7609 StartY=53.0133 StartZ=0 EndX=-34.7333 EndY=42.214 EndZ=0
    g19: ArcOfCircle CenterX=-32.5 CenterY=43.2537 CenterZ=0 NormalX=0 NormalY=0 NormalZ=1 AngleXU=0 Radius=2.46346 StartAngle=3.57731 EndAngle=5.84747
    g20: ArcOfCircle CenterX=-23.6979 CenterY=38.9017 CenterZ=0 NormalX=0 NormalY=0 NormalZ=1 AngleXU=0 Radius=2.93861 StartAngle=2.70588 EndAngle=4.71239
    g21: ArcOfCircle CenterX=-39.6179 CenterY=39.6956 CenterZ=0 NormalX=0 NormalY=0 NormalZ=1 AngleXU=0 Radius=2.07559 StartAngle=4.26997 EndAngle=6.83089
    g22: LineSegment [constr] StartX=-32.5 StartY=33.2903 StartZ=0 EndX=-32.5 EndY=43.2537 EndZ=0
    g23: LineSegment StartX=-43.218 StartY=49.584 StartZ=0 EndX=-47.1952 EndY=40.9886 EndZ=0
    g24: LineSegment [constr] StartX=0 StartY=33.2903 StartZ=0 EndX=-16.25 EndY=33.2903 EndZ=0
    g25: LineSegment [constr] StartX=-16.25 StartY=33.2903 StartZ=0 EndX=-32.5 EndY=33.2903 EndZ=0
    g26: LineSegment [constr] StartX=-14.45 StartY=35.9631 StartZ=0 EndX=-16.25 EndY=33.2903 EndZ=0
    g27: LineSegment [constr] StartX=-18.05 StartY=35.9631 StartZ=0 EndX=-16.25 EndY=33.2903 EndZ=0
    g28: ArcOfCircle CenterX=-8.8021 CenterY=38.9017 CenterZ=0 NormalX=0 NormalY=0 NormalZ=1 AngleXU=0 Radius=2.93861 StartAngle=4.71239 EndAngle=6.7189
    g29: LineSegment StartX=0 StartY=53.0133 StartZ=0 EndX=-7.26094 EndY=53.0133 EndZ=0
    g30: LineSegment StartX=-7.26094 StartY=53.0133 StartZ=0 EndX=-2.23329 EndY=42.214 EndZ=0
    g31: ArcOfCircle CenterX=1.55717e-07 CenterY=43.2537 CenterZ=0 NormalX=0 NormalY=0 NormalZ=1 AngleXU=0 Radius=2.46346 StartAngle=3.57731 EndAngle=5.84747
    g32: LineSegment [constr] StartX=-39.7609 StartY=53.0133 StartZ=0 EndX=0 EndY=53.0133 EndZ=0
    g33: LineSegment StartX=-18.05 StartY=53.0133 StartZ=0 EndX=-20.3696 EndY=53.0133 EndZ=0
    g34: LineSegment StartX=-12.1304 StartY=53.0133 StartZ=0 EndX=-14.45 EndY=53.0133 EndZ=0
    g35: LineSegment StartX=-6.13805 StartY=40.1419 StartZ=0 EndX=-12.1304 EndY=53.0133 EndZ=0
    g36: LineSegment [constr] StartX=-47.1952 StartY=40.9886 StartZ=0 EndX=-47.1952 EndY=36.1192 EndZ=0
    g37: LineSegment StartX=-47.1952 StartY=36.1192 StartZ=0 EndX=-47.1952 EndY=30.4614 EndZ=0
    g38: LineSegment StartX=-41.5183 StartY=35.1042 StartZ=0 EndX=-47.1952 EndY=36.1192 EndZ=0
    g39: ArcOfCircle CenterX=-41.8427 CenterY=33.2903 CenterZ=0 NormalX=0 NormalY=0 NormalZ=1 AngleXU=0 Radius=1.84266 StartAngle=4.88932 EndAngle=7.67705
    g40: Circle [constr] CenterX=-32.5 CenterY=33.2903 CenterZ=0 NormalX=0 NormalY=0 NormalZ=1 AngleXU=0 Radius=9.19895
    g41: Circle [constr] CenterX=0 CenterY=33.2903 CenterZ=0 NormalX=0 NormalY=0 NormalZ=1 AngleXU=0 Radius=9.19895
    g42: LineSegment StartX=2.23329 StartY=42.214 StartZ=0 EndX=7.26094 EndY=53.0133 EndZ=0
    g43: LineSegment StartX=7.26094 StartY=53.0133 StartZ=0 EndX=0 EndY=53.0133 EndZ=0
    g44: LineSegment StartX=-41.5183 StartY=31.4764 StartZ=0 EndX=-47.1952 EndY=30.4614 EndZ=0
    g45: LineSegment [constr] StartX=-25.2391 StartY=53.0133 StartZ=0 EndX=-20.3696 EndY=53.0133 EndZ=0
    g46: LineSegment [constr] StartX=-12.1304 StartY=53.0133 StartZ=0 EndX=-7.26094 EndY=53.0133 EndZ=0
  constraints (126):
    c: DistanceX(g0) = 25.0019
    c: DistanceY(g0) = 15.3639
    c: DistanceX(g0) = 40
    c: DistanceY(g0) = 24.4135
    c: DistanceX(g1,g1) = 80
    c: Symmetric(g1,g1,g-2)
    c: DistanceY(g1) = 33.2903
    c: PointOnObject(g2,g1)
    c: PointOnObject(g3,g-2)
    c: PointOnObject(g3,g1)
    c: Coincident(g4,g2)
    c: PointOnObject(g1,g4)
    c: Coincident(g5,g3)
    c: Horizontal(g9)
    c: Vertical(g10)
    c: Coincident(g12,g6)
    c: Vertical(g13)
    c: Coincident(g14,g13)
    c: Horizontal(g14)
    c: Coincident(g15,g13)
    c: Horizontal(g15)
    c: Coincident(g10,g9)
    c: Coincident(g15,g9)
    c: Coincident(g12,g11)
    c: Coincident(g16,g17)
    c: Coincident(g17,g18)
    c: Tangent(g16,g19) = -1.5708
    c: Tangent(g18,g19) = -1.5708
    c: Tangent(g8,g20) = 1.5708
    c: Tangent(g9,g20) = -1.5708
    c: DistanceX(g6) = -47.1952
    c: DistanceY(g6) = 40.9886
    c: DistanceX(g11) = -39.7609
    c: DistanceY(g11) = 53.0133
    c: Tangent(g6,g21) = 1.5708
    c: Tangent(g7,g21) = -1.5708
    c: Coincident(g7,g11)
    c: Coincident(g17,g11)
    c: Coincident(g22,g2)
    c: Coincident(g22,g19)
    c: Vertical(g22)
    c: Coincident(g23,g7)
    c: Coincident(g23,g6)
    c: Coincident(g24,g3)
    c: Coincident(g25,g24)
    c: Coincident(g25,g2)
    c: Equal(g24,g25)
    c: Horizontal(g24)
    c: Coincident(g26,g13)
    c: Coincident(g27,g9)
    c: Coincident(g27,g24)
    c: Coincident(g24,g26)
    c: Equal(g27,g26)
    c: Tangent(g14,g28) = 1.5708
    c: Equal(g9,g14)
    c: Tangent(g21,g4)
    c: Tangent(g19,g4)
    c: Tangent(g20,g4)
    c: Horizontal(g29)
    c: Coincident(g29,g30)
    c: Tangent(g31,g30)
    c: Coincident(g31,g30)
    c: PointOnObject(g32,g-2)
    c: Horizontal(g32)
    c: PointOnObject(g29,g32)
    c: Horizontal(g17)
    c: Coincident(g33,g10)
    c: Coincident(g33,g8)
    c: Horizontal(g33)
    c: Coincident(g34,g13)
    c: Horizontal(g34)
    c: Coincident(g32,g11)
    c: DistanceX(g15,g15) = 3.6
    c: Parallel(g8,g16)
    c: Coincident(g35,g28)
    c: Coincident(g35,g34)
    c: Tangent(g35,g28)
    c: Equal(g33,g34)
    c: PointOnObject(g34,g32)
    c: PointOnObject(g10,g32)
    c: Coincident(g36,g6)
    c: Coincident(g38,g37)
    c: Coincident(g39,g38)
    c: Tangent(g39,g38)
    c: PointOnObject(g7,g40)
    c: PointOnObject(g18,g40)
    c: PointOnObject(g16,g40)
    c: PointOnObject(g8,g40)
    c: PointOnObject(g6,g40)
    c: Coincident(g41,g3)
    c: PointOnObject(g30,g41)
    c: PointOnObject(g28,g41)
    c: PointOnObject(g14,g41)
    c: Tangent(g28,g5)
    c: Equal(g41,g40)
    c: Parallel(g30,g35)
    c: PointOnObject(g38,g40)
    c: PointOnObject(g31,g41)
    c: Tangent(g31,g5)
    c: Coincident(g42,g31)
    c: Tangent(g42,g31)
    c: Coincident(g43,g42)
    c: Coincident(g43,g29)
    c: Equal(g43,g29)
    c: Coincident(g44,g39)
    c: PointOnObject(g39,g40)
    c: Tangent(g44,g39)
    c: Tangent(g39,g4)
    c: Coincident(g37,g44)
    c: Symmetric(g37,g37,g1)
    c: PointOnObject(g37,g36)
    c: Equal(g2,g3)
    c: Coincident(g36,g37)
    c: DistanceX(g7) = -43.218
    c: DistanceY(g7) = 49.584
    c: Radius(g5) = 7.5
    c: Radius(g3) = 4.05
    c: Coincident(g45,g16)
    c: Coincident(g45,g8)
    c: Coincident(g46,g34)
    c: Coincident(g46,g29)
    c: Equal(g45,g46)
    c: Symmetric(g29,g42,g-2)
    c: PointOnObject(g9,g40)
    c: Equal(g45,g11)
    c: Equal(g11,g36)
FEATURE [Part::Feature] Path003  label="Path28D40L"
  Placement = pos=(-47.2032,52.9993,0) rot=(0,0,1;0rad)
  shape: bbox 94.81 x 38.58 x 2e-07 mm, 0 faces, 0 solids (baked)
FEATURE [Sketcher::SketchObject] Sketch012014
  MapMode = 5
  expr: Constraints[3] = 0.5 * Spreadsheet.AxisD + Spreadsheet.HolesClearance + 2 * Spreadsheet.HoldingEdge
  expr: Constraints[2] = 0.5 * (Spreadsheet.AxisD + Spreadsheet.HolesClearance)
  sketch-geometry (2):
    g0: Circle CenterX=0 CenterY=0 CenterZ=0 NormalX=0 NormalY=0 NormalZ=1 AngleXU=0 Radius=4.05
    g1: Circle CenterX=0 CenterY=0 CenterZ=0 NormalX=0 NormalY=0 NormalZ=1 AngleXU=0 Radius=6.5
  constraints (4):
    c: Coincident(g0,g-1)
    c: Coincident(g1,g-1)
    c: Radius(g0) = 4.05
    c: Radius(g1) = 6.5
FEATURE [PartDesign::Pad] Pad004002019  label="TestSleeve"
  Length = 10
  Length2 = 100
  Profile = -> Sketch012014
  Type = 0
  expr: Length = 2 * Spreadsheet.BearingDepth
FEATURE [Mesh::Feature] Mesh003  label="Test-sleeve"
FEATURE [Mesh::Feature] Mesh004  label="WholeLink-v5"
FEATURE [Part::Extrusion] Extrude001  label="RailCutoutElement"
  Base = -> Sketch012013
  Dir = (0,0,50)
  DirMode = 0
  FaceMakerClass = Part::FaceMakerExtrusion
  LengthFwd = 0
  LengthRev = 0
  Solid = true
  Symmetric = true
FEATURE [Part::Mirroring] Part__Mirroring  label="RailCutoutElementMirror1"
  Base = (0,0,0)
  Normal = (1,0,0)
  Source = -> Extrude001
FEATURE [Part::Mirroring] Part__Mirroring001  label="RailCutoutElementMirror2"
  Base = (0,33.291,0)
  Normal = (0,1,0)
  Source = -> Extrude001
FEATURE [Part::Mirroring] Part__Mirroring002  label="RailCutoutElementMirror2 (Mirror #3)"
  Base = (0,0,0)
  Normal = (1,0,0)
  Source = -> Part__Mirroring001
FEATURE [Part::MultiFuse] Fusion003  label="RailCutoutUnion"
  Shapes = -> [Extrude001,Part__Mirroring,Part__Mirroring001,Part__Mirroring002]
FEATURE [Sketcher::SketchObject] Sketch012015  label="RailsMiddleSketch"
  MapMode = 2
  Support = -> [Sketch012013]
  expr: Constraints[3] = Spreadsheet.RailCenterY
  sketch-geometry (12):
    g0: LineSegment [constr] StartX=26.5 StartY=16 StartZ=0 EndX=39.9 EndY=24.2942 EndZ=0
    g1: LineSegment [constr] StartX=39.9 StartY=33.2903 StartZ=0 EndX=0 EndY=33.2903 EndZ=0
    g2: LineSegment StartX=32.4 StartY=40.7903 StartZ=0 EndX=26.5 EndY=50.5806 EndZ=0
    g3: LineSegment StartX=26.5 StartY=50.5806 StartZ=0 EndX=-26.5 EndY=50.5806 EndZ=0
    g4: LineSegment StartX=-26.5 StartY=50.5806 StartZ=0 EndX=-32.4 EndY=40.7903 EndZ=0
    g5: LineSegment StartX=-32.4 StartY=25.7903 StartZ=0 EndX=-26.5 EndY=16 EndZ=0
    g6: LineSegment StartX=-26.5 StartY=16 StartZ=0 EndX=26.5 EndY=16 EndZ=0
    g7: ArcOfCircle CenterX=-32.4 CenterY=33.2903 CenterZ=0 NormalX=0 NormalY=0 NormalZ=1 AngleXU=0 Radius=7.5 StartAngle=1.5708 EndAngle=4.71239
    g8: ArcOfCircle CenterX=32.4 CenterY=33.2903 CenterZ=0 NormalX=0 NormalY=0 NormalZ=1 AngleXU=0 Radius=7.5 StartAngle=4.71239 EndAngle=7.85398
    g9: LineSegment [constr] StartX=39.9 StartY=24.2942 StartZ=0 EndX=39.9 EndY=33.2903 EndZ=0
    g10: LineSegment StartX=32.4 StartY=25.7903 StartZ=0 EndX=26.5 EndY=16 EndZ=0
    g11: LineSegment [constr] StartX=-32.4 StartY=40.7903 StartZ=0 EndX=-32.4 EndY=25.7903 EndZ=0
  constraints (32):
    c: DistanceY(g0) = 16
    c: Horizontal(g1)
    c: PointOnObject(g1,g-2)
    c: DistanceY(g1) = 33.2903
    c: Coincident(g2,g3)
    c: Coincident(g3,g4)
    c: Coincident(g5,g6)
    c: Coincident(g6,g0)
    c: Symmetric(g0,g2,g1)
    c: Symmetric(g0,g5,g-2)
    c: DistanceY(g0) = 24.2942
    c: Coincident(g7,g4)
    c: PointOnObject(g1,g8)
    c: Coincident(g9,g0)
    c: Vertical(g9)
    c: Coincident(g9,g1)
    c: Radius(g8) = 7.5
    c: Angle(g8) = 3.14159
    c: Coincident(g8,g2)
    c: Coincident(g10,g6)
    c: Coincident(g7,g5)
    c: Angle(g7) = 3.14159
    c: Coincident(g10,g8)
    c: Symmetric(g8,g2,g1)
    c: Symmetric(g8,g7,g-2)
    c: Symmetric(g3,g2,g-2)
    c: DistanceX(g1,g1) = 39.9
    c: DistanceX(g3,g3) = 53
    c: Equal(g7,g8)
    c: Coincident(g11,g4)
    c: Coincident(g11,g5)
    c: Vertical(g11)
FEATURE [Part::Extrusion] Extrude
  Base = -> Sketch012015
  Dir = (0,0,1)
  DirMode = 0
  FaceMakerClass = Part::FaceMakerBullseye
  LengthFwd = 18.7
  LengthRev = 0
  Solid = true
  Symmetric = true
  expr: LengthFwd = 9.35 * 2
FEATURE [Part::Cut] Cut007  label="RailsMiddle"
  Base = -> Extrude
  Tool = -> Fusion003
FEATURE [Part::FeaturePython] Clone036  label="WholeLink0"  # Draft clone (typed FeaturePython)
  AttacherType = Attacher::AttachEngine3D
  Fuse = false
  Objects = -> [Chamfer]
  Scale = (1,1,1)
FEATURE [Part::FeaturePython] Clone037  label="Axle0"  # Draft clone (typed FeaturePython)
  AttacherType = Attacher::AttachEngine3D
  Fuse = false
  Objects = -> [Compound]
  Scale = (1,1,1)
FEATURE [Part::FeaturePython] Clone038  label="WholeLink3"  # Draft clone (typed FeaturePython)
  AttacherType = Attacher::AttachEngine3D
  Fuse = false
  Objects = -> [Chamfer]
  Placement = pos=(40,66.5806,0) rot=(0,0,1;3.14159rad)
  Scale = (1,1,1)
  expr: Placement.Base.x = Spreadsheet.LinkLength
  expr: Placement.Base.y = Spreadsheet.RailCenterY * 2
FEATURE [Part::FeaturePython] Clone039  label="Axle4"  # Draft clone (typed FeaturePython)
  AttacherType = Attacher::AttachEngine3D
  Fuse = false
  Objects = -> [Compound]
  Placement = pos=(0,66.5806,0) rot=(0,0,1;0rad)
  Scale = (1,1,1)
  expr: Placement.Base.y = Spreadsheet.RailCenterY * 2
FEATURE [Part::FeaturePython] Clone040  label="WholeLink4"  # Draft clone (typed FeaturePython)
  AttacherType = Attacher::AttachEngine3D
  Fuse = false
  Objects = -> [Chamfer]
  Placement = pos=(0,66.5806,0) rot=(0,0,1;3.14159rad)
  Scale = (1,1,1)
  expr: Placement.Base.y = Spreadsheet.RailCenterY * 2
FEATURE [Part::FeaturePython] Clone041  label="Axle5"  # Draft clone (typed FeaturePython)
  AttacherType = Attacher::AttachEngine3D
  Fuse = false
  Objects = -> [Compound]
  Placement = pos=(-40,66.5806,0) rot=(0,0,1;0rad)
  Scale = (1,1,1)
  expr: Placement.Base.x = -Spreadsheet.LinkLength
  expr: Placement.Base.y = Spreadsheet.RailCenterY * 2
FEATURE [Part::FeaturePython] Clone042  label="Axle6"  # Draft clone (typed FeaturePython)
  AttacherType = Attacher::AttachEngine3D
  Fuse = false
  Objects = -> [Compound]
  Placement = pos=(-62.1756,33.2903,0) rot=(0,0,1;0rad)
  Scale = (1,1,1)
  expr: Placement.Base.x = -Spreadsheet.LinkLength * (1 + cos(Spreadsheet.OptimalEllipseAngle))
  expr: Placement.Base.y = Spreadsheet.RailCenterY
FEATURE [Part::FeaturePython] Clone043  label="Axle7"  # Draft clone (typed FeaturePython)
  AttacherType = Attacher::AttachEngine3D
  Fuse = false
  Objects = -> [Compound]
  Placement = pos=(-40,0,0) rot=(0,0,1;0rad)
  Scale = (1,1,1)
  expr: Placement.Base.x = -Spreadsheet.LinkLength
FEATURE [Part::FeaturePython] Clone044  label="WholeLink5"  # Draft clone (typed FeaturePython)
  AttacherType = Attacher::AttachEngine3D
  Fuse = false
  Objects = -> [Chamfer]
  Placement = pos=(-40,66.5806,0) rot=(0,0,1;4.12476rad)
  Scale = (1,1,1)
  expr: Placement.Rotation.Angle = 180 + Spreadsheet.OptimalEllipseAngle
  expr: Placement.Base.x = -Spreadsheet.LinkLength
  expr: Placement.Base.y = Spreadsheet.RailCenterY * 2
FEATURE [Part::FeaturePython] Clone045  label="WholeLink6"  # Draft clone (typed FeaturePython)
  AttacherType = Attacher::AttachEngine3D
  Fuse = false
  Objects = -> [Chamfer]
  Placement = pos=(-62.1756,33.2903,0) rot=(0,0,-1;7.26635rad)
  Scale = (1,1,1)
  expr: Placement.Rotation.Angle = 360 + Spreadsheet.OptimalEllipseAngle
  expr: Placement.Base.x = -Spreadsheet.LinkLength * (1 + cos(Spreadsheet.OptimalEllipseAngle))
  expr: Placement.Base.y = Spreadsheet.RailCenterY
FEATURE [Part::Extrusion] Extrude002  label="RailSideContour"
  Base = -> Sketch012015
  Dir = (0,0,1)
  DirMode = 2
  FaceMakerClass = Part::FaceMakerBullseye
  LengthFwd = 2.5
  LengthRev = 0
  Solid = true
  Symmetric = false
  expr: LengthFwd = 0.5 * Spreadsheet.BearingDepth
FEATURE [Sketcher::SketchObject] Sketch012016
  Placement = pos=(0,0,0) rot=(0.57735,0.57735,0.57735;2.0944rad)
  expr: Constraints[10] = 0.5 * Spreadsheet.BearingDepth
  expr: Constraints[7] = Spreadsheet.RailCenterY
  sketch-geometry (5):
    g0: LineSegment StartX=16.2903 StartY=0 StartZ=0 EndX=25.2903 EndY=2.5 EndZ=0
    g1: LineSegment StartX=25.2903 StartY=2.5 StartZ=0 EndX=41.2903 EndY=2.5 EndZ=0
    g2: LineSegment StartX=41.2903 StartY=2.5 StartZ=0 EndX=50.2903 EndY=0 EndZ=0
    g3: LineSegment StartX=16.2903 StartY=0 StartZ=0 EndX=50.2903 EndY=0 EndZ=0
    g4: GeomPoint X=33.2903 Y=0 Z=0
  constraints (13):
    c: PointOnObject(g0,g-1)
    c: Coincident(g0,g1)
    c: Horizontal(g1)
    c: Coincident(g1,g2)
    c: PointOnObject(g2,g-1)
    c: Coincident(g0,g3)
    c: Coincident(g3,g2)
    c: DistanceX(g4) = 33.2903
    c: Symmetric(g0,g2,g4)
    c: Equal(g0,g2)
    c: DistanceY(g0) = 2.5
    c: DistanceX(g1,g1) = 16
    c: DistanceX(g3,g3) = 34
FEATURE [Part::Extrusion] Extrude003  label="RailSideProfile"
  Base = -> Sketch012016
  Dir = (1,0,0)
  DirMode = 2
  FaceMakerClass = Part::FaceMakerBullseye
  LengthFwd = 100
  LengthRev = 0
  Solid = true
  Symmetric = true
FEATURE [Part::MultiCommon] Common002  label="RailSideExt"
  Placement = pos=(0,0,15.3) rot=(0,0,1;0rad)
  Shapes = -> [Extrude002,Extrude003]
  expr: Placement.Base.z = Spreadsheet.SpacerDepth + Spreadsheet.BearingDepth
FEATURE [Part::MultiFuse] Fusion004  label="RailSideSolid"
  Shapes = -> [Common002,Loft]
FEATURE [Part::Cut] Cut006  label="RailsTopSide"
  Base = -> Fusion004
  Tool = -> Fusion003
FEATURE [Part::Mirroring] Part__Mirroring003  label="RailsBottom"
  Base = (0,0,0)
  Normal = (0,0,1)
  Source = -> Cut006
FEATURE [Part::Compound] Compound001  label="RailsAssembly"
  Links = -> [Cut007,Part__Mirroring003,Cut006]
FEATURE [Part::Extrusion] Extrude004  label="TestRailTrussCutout"
  Base = -> Sketch012007
  Dir = (0,-1,2e-16)
  DirMode = 2
  FaceMakerClass = Part::FaceMakerBullseye
  LengthFwd = 50
  LengthRev = 0
  Solid = true
  Symmetric = true
FEATURE [Part::Fillet] Fillet  label="TestRailCutoutSmoothed"
  Base = -> Extrude004
  Edges = 8 edges r=1: [Edge2,Edge5,Edge10,Edge14,Edge19,Edge23,Edge29,Edge32]
FEATURE [Part::FeaturePython] Array001  label="TestRailCutoutArray"  # Draft array (typed FeaturePython)
  Angle = 360
  ArrayType = 0
  Axis = (0,0,1)
  Base = -> Fillet
  Center = (0,0,0)
  Fuse = false
  IntervalAxis = (0,0,0)
  IntervalX = (26,0,0)
  IntervalY = (0,0,0)
  IntervalZ = (0,0,0)
  NumberPolar = 1
  NumberX = 8
  NumberY = 1
  NumberZ = 1
  Placement = pos=(-130,0,0) rot=(0,0,1;0rad)
FEATURE [Part::Cut] Cut001  label="TestRail"
  Base = -> Pad004002016
  Tool = -> Array001
FEATURE [App::DocumentObjectGroup] Group005  label="MeshesToPrint"
  Group = -> [Mesh001,Mesh002,Mesh003,Mesh004,Cut006]
FEATURE [Part::FeaturePython] Clone  label="Rails"  # Draft clone (typed FeaturePython)
  AttacherType = Attacher::AttachEngine3D
  Fuse = false
  Objects = -> [Compound001]
  Scale = (1,1,1)
FEATURE [App::DocumentObjectGroup] Group004  label="FullAssemblyPreview"
  Group = -> [Clone031,Clone032,Clone033,Clone034,Clone035,Clone028,Clone036,Clone037,Clone038,Clone039,Clone040,Clone041,Clone042,Clone043,Clone044,Clone045,Clone]
FEATURE [App::DocumentObjectGroup] Group006  label="Testing"
  Group = -> [Pad004002019,Sketch012011,Cut001]
